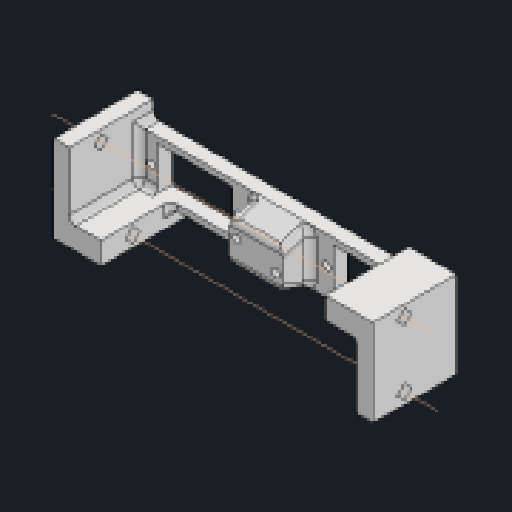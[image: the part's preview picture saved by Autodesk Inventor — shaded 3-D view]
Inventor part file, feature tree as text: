
AUTODESK INVENTOR PART (.ipt)
format: ipt  version: 2023.2 (Build 272271030, 271C)  size: 681,472 bytes
history: native  units: mm
features: sketch x7, projected_geometry x6, extrude x5, chamfer x3, hole x2, other x2, fillet x1
ambient origin geometry x8: Origin, YZ Plane, XZ Plane, XY Plane, X Axis, Y Axis, Z Axis, Center Point
bodies: Solid1 (feature_tree)
feature tree (26):
  extrude  "Extrusion1"  Depth=27.5mm
  extrude  "Extrusion2"  Depth=13.5mm
  hole  "Hole1"  [1 undecoded]
  extrude  "Extrusion4"  Depth=7.0mm
  extrude  "Extrusion3"  Depth=7.0mm
  chamfer  "Chamfer1"  Distance=5.0mm
  hole  "Hole2"  [1 undecoded]
  sketch  "Sketch6"  dims[d11=5.0mm]
  fillet  "Fillet2"  Radius=27.8mm
  extrude  "Extrusion5"  Depth=3.5mm
  other  "Work Axis1"
  other  "Work Axis2"
  chamfer  "Chamfer3"  Distance=17.0mm
  chamfer  "Chamfer4"  Distance=8.5mm
  sketch  "Sketch1"  dims[d0=101.0mm d1=27.5mm]
  sketch  "Sketch2"  dims[d2=7.0mm d3=13.5mm]
  projected_geometry  "Projected Loop1"
  sketch  "Sketch3"  dims[d4=11.0mm d5=11.0mm]
  projected_geometry  "Projected Loop2"
  sketch  "Sketch4"  dims[d6=23.5mm d7=7.0mm]
  projected_geometry  "Projected Loop3"
  sketch  "Sketch5"  dims[d8=5.0mm d9=0.0mm d10=7.0mm]
  projected_geometry  "Projected Loop4"
  projected_geometry  "Projected Loop5"
  sketch  "Sketch7"  dims[d12=15.0mm d13=5.0mm d14=22.0mm d15=0.0mm d16=27.8mm d17=2.5mm d18=6.0mm d19=5.5mm d20=25.45mm d21=90.0deg d22=8.0mm d23=20.594885mm d24=7.0mm d25=17.0mm d26=8.5mm d27=0.0mm d28=3.0mm d29=8.5mm d30=45.0deg d31=6.6mm d32=16.5mm d33=6.6mm d34=12.125mm d35=12.125mm d36=2.5mm d37=6.0mm d38=3.7mm d39=3.5mm d40=90.0deg d41=8.0mm d42=20.594885mm d43=20.5mm d45=3.5mm d46=3.5mm d58=18.0mm d59=2.0mm d60=2.0mm d61=22.0mm d62=0.0mm d63=2.0mm d64=3.3mm d65=0.0mm d66=0.0mm d67=0.5mm d68=2.0mm d69=45.0deg d70=1.0mm d71=2.0mm d72=45.0deg]
  projected_geometry  "Projected Loop6"
note: 2 required parameter values undecoded (feature->parameter linkage not recoverable at this tier; creation-order binding heuristic only, values carry confidence <= 0.55)
